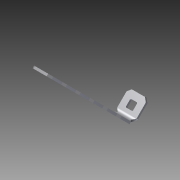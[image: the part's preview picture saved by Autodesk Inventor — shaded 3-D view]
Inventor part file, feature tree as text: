
AUTODESK INVENTOR PART (.ipt)
format: ipt  version: 2014 SP1 (Build 180222100, 222)  size: 602,112 bytes
history: native  units: in
note: dims shown in document units (in); Inventor stores cm internally (conversion verified against a paired STEP export)
features: other x2, sketch x2, imported_body x1, extrude x1
ambient origin geometry x8: Origin, YZ Plane, XZ Plane, XY Plane, X Axis, Y Axis, Z Axis, Center Point
bodies: Body1 (feature_tree)
feature tree (6):
  parser-record x1  (decoder bookkeeping rows leaked as tree rows — omitted from the tree; the rows remain in map.json)
  imported_body  "Base1"
  extrude  "Extrusion1"  Depth=1.0in TaperAngle=0.0deg
  other  "Bend Part1"
  sketch  "Sketch1"  dims[d0=3.5in d1=1.0in d2=0.0in]
  sketch  "Sketch2"  dims[d3=0.1in d4=90.0deg]
